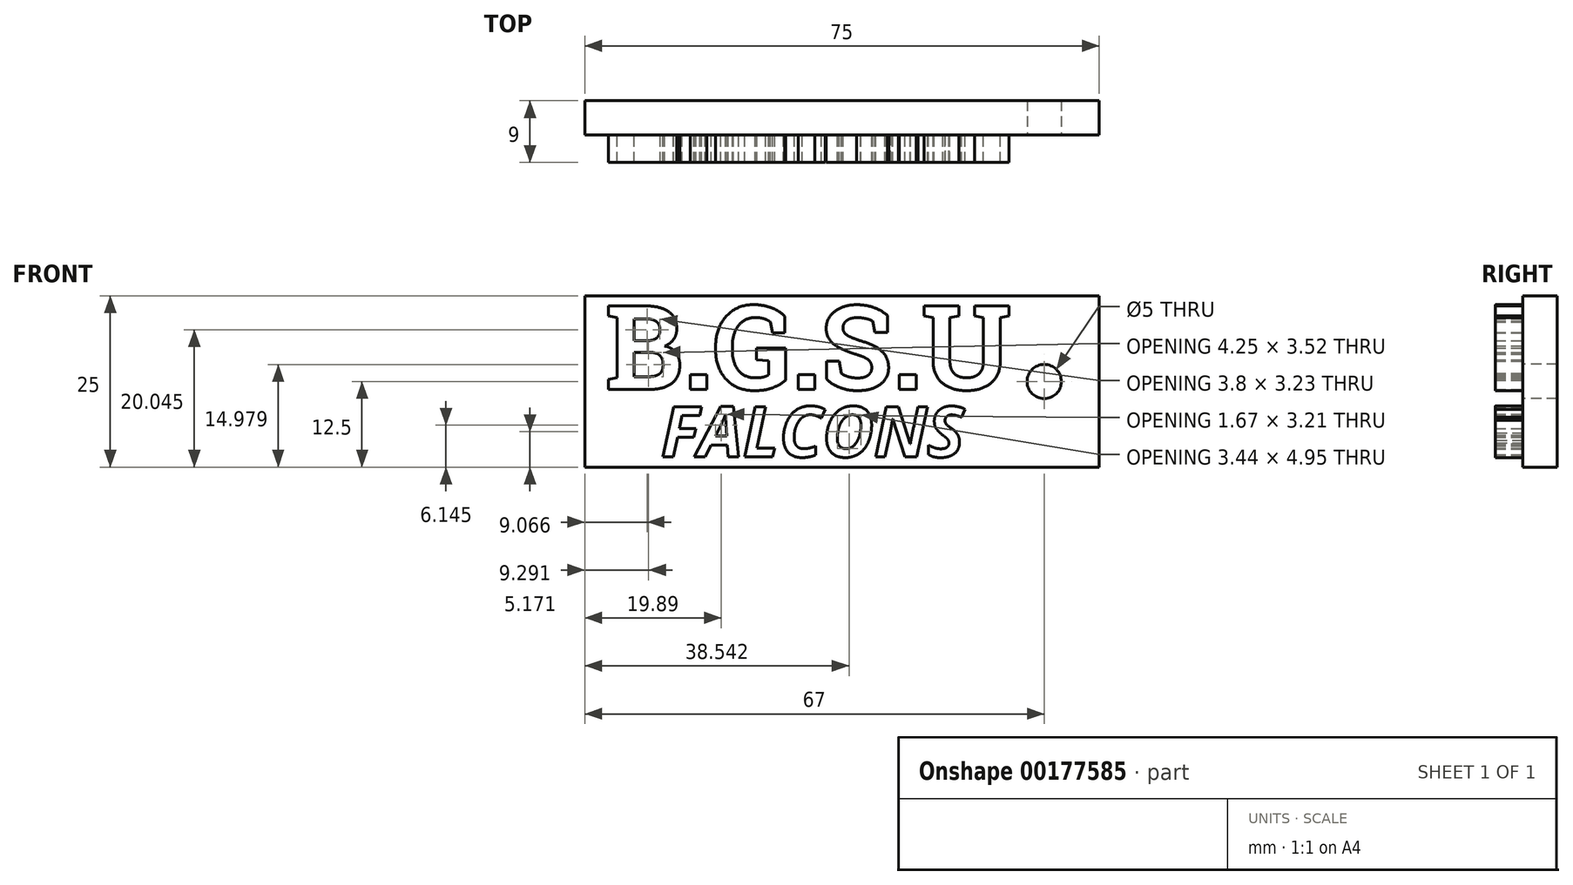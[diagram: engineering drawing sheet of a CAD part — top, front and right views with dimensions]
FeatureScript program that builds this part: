
annotation { "Feature Type Name" : "Feature", "Feature Type Description" : "" }
export const myFeature = defineFeature(function(context is Context, id is Id, definition is map)
    precondition{}
    {
        {
            var Q0;
            Q0=qCreatedBy(makeId("Front.planeOp"),FACE);
            var sketch = newSketch(context, id + "F0", { "sketchPlane" : qUnion([Q0])});
            skLineSegment(sketch, "E0.bottom", {"start": v(0, 0) * mm, "end": v(75, 0) * mm});
            skLineSegment(sketch, "E0.top", {"start": v(0, -25) * mm, "end": v(75, -25) * mm});
            skLineSegment(sketch, "E0.left", {"start": v(0, 0) * mm, "end": v(0, -25) * mm});
            skLineSegment(sketch, "E0.right", {"start": v(75, 0) * mm, "end": v(75, -25) * mm});
            skCircle(sketch, "E1", {"center": v(67, -12.5) * mm, "radius": 2.5 * mm});
            skSolve(sketch);
        }
        {
            var Q0;
            Q0=makeQuery(id+"F0.imprint","IMPRINT",FACE,{"disambiguationData":[TD([[makeQuery(id+"F0.imprint","IMPRINT",EDGE,{"derivedFrom":sQuery(id+"F0.wireOp",EDGE,"E0.bottom")}),-1.0]])]});
            var sketch = newSketch(context, id + "F1", { "sketchPlane" : qUnion([Q0])});
            skText(sketch, "E2", { "text": "B.G.S.U", "fontName": "RobotoSlab-Bold.ttf"});
            skText(sketch, "E3", { "text": "FALCONS", "fontName": "OpenSans-BoldItalic.ttf"});
            const initialGuessF1  = {"E2": [0.00295, -0.01366, 1, 0, 0.01236], "E3": [0.01112, -0.02351, 1, 0, 0.0074]};
            skSetInitialGuess(sketch, initialGuessF1);
            skSolve(sketch);
        }
        {
            var Q0;
            Q0 = qSketchRegion(id + "F1", true);
            extrude(context, id + "F2", {"entities" : qUnion([Q0]), "depth" : 4 * mm});
        }
        {
            var Q0;
            Q0=makeQuery(id+"F0.imprint","IMPRINT",FACE,{"disambiguationData":[TD([[makeQuery(id+"F0.imprint","IMPRINT",EDGE,{"derivedFrom":sQuery(id+"F0.wireOp",EDGE,"E0.bottom")}),-1.0]])]});
            extrude(context, id + "F3", {"entities" : qUnion([Q0]), "oppositeDirection" : true, "depth" : 5 * mm});
        }
    });
